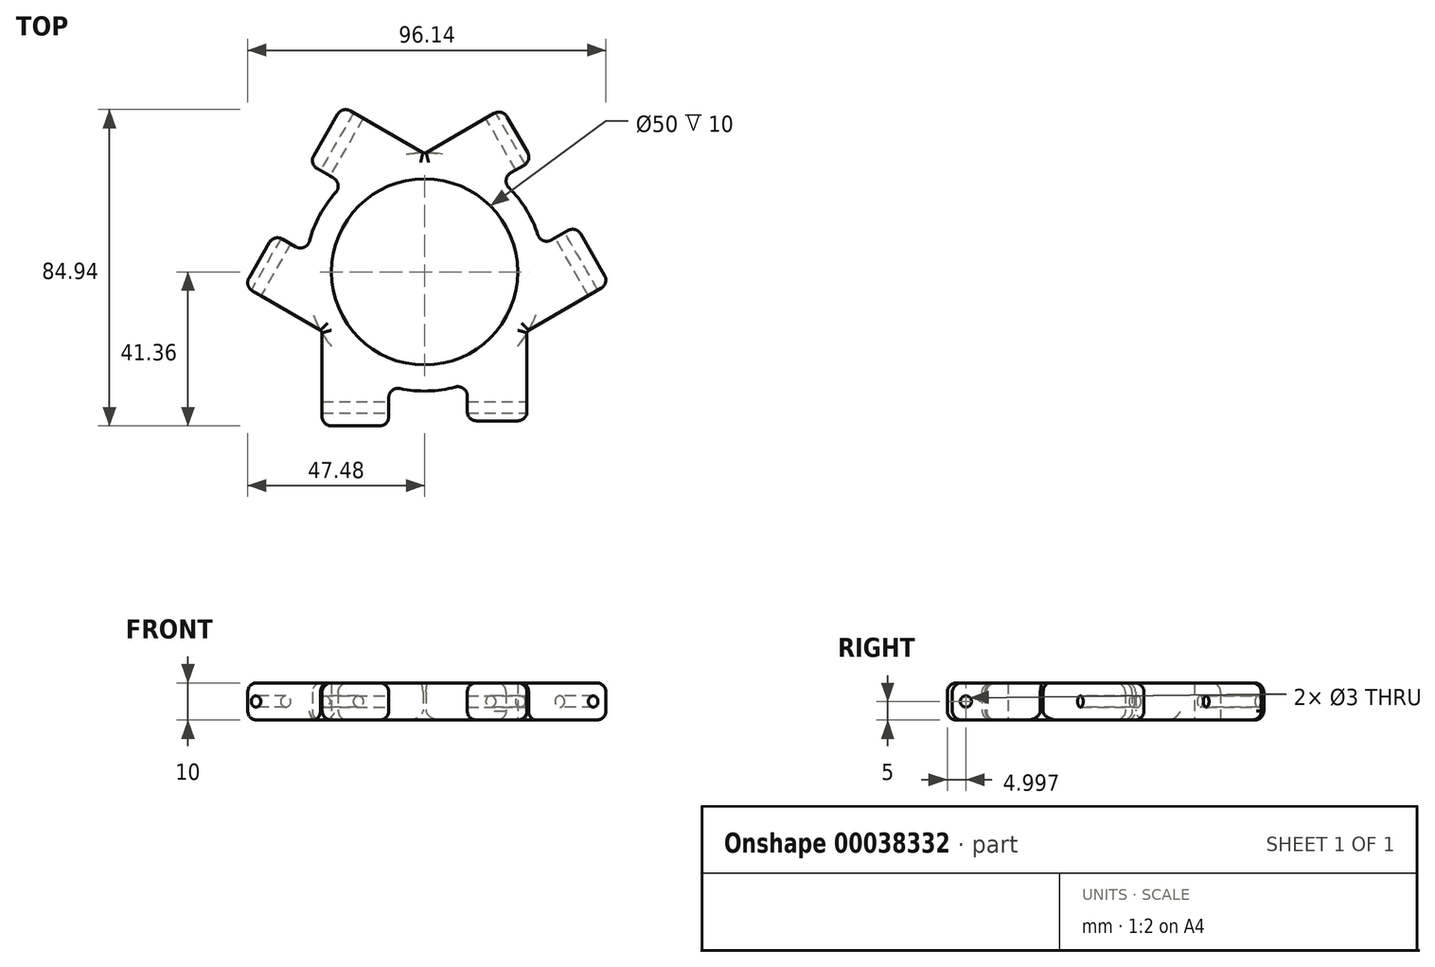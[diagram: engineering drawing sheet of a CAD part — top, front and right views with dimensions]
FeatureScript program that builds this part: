
annotation { "Feature Type Name" : "Feature", "Feature Type Description" : "" }
export const myFeature = defineFeature(function(context is Context, id is Id, definition is map)
    precondition{}
    {
        {
            var Q0;
            Q0=qCreatedBy(makeId("Top.planeOp"),FACE);
            var sketch = newSketch(context, id + "F0", { "sketchPlane" : qUnion([Q0])});
            skCircle(sketch, "E0", {"center": v(0, 0) * mm, "radius": 25 * mm});
            skCircle(sketch, "E1", {"center": v(0, 0) * mm, "radius": 32 * mm});
            skLineSegment(sketch, "E2", {"start": v(-9.6, -41.36) * mm, "end": v(-9.6, -30.53) * mm});
            skLineSegment(sketch, "E3", {"start": v(11.45, -29.88) * mm, "end": v(11.45, -40) * mm});
            skLineSegment(sketch, "E4", {"start": v(-27.5, -41.36) * mm, "end": v(-9.6, -41.36) * mm});
            skLineSegment(sketch, "E5", {"start": v(11.45, -40) * mm, "end": v(27.5, -40) * mm});
            skLineSegment(sketch, "E6", {"start": v(27.5, -40) * mm, "end": v(27.5, -16.36) * mm});
            skLineSegment(sketch, "E7", {"start": v(-27.5, -41.36) * mm, "end": v(-27.5, -16.36) * mm});
            skLineSegment(sketch, "E8.1.0", {"start": v(28.91, 29.92) * mm, "end": v(20.9, 43.82) * mm});
            skLineSegment(sketch, "E8.1.1", {"start": v(49.57, -3.13) * mm, "end": v(27.92, -15.63) * mm});
            skLineSegment(sketch, "E8.1.2", {"start": v(49.57, -3.13) * mm, "end": v(40.62, 12.37) * mm});
            skLineSegment(sketch, "E8.1.3", {"start": v(20.9, 43.82) * mm, "end": v(0.42, 32) * mm});
            skLineSegment(sketch, "E8.1.4", {"start": v(20.15, 24.86) * mm, "end": v(28.91, 29.92) * mm});
            skLineSegment(sketch, "E8.1.5", {"start": v(40.62, 12.37) * mm, "end": v(31.24, 6.95) * mm});
            skLineSegment(sketch, "E8.2.0", {"start": v(-40.37, 10.08) * mm, "end": v(-48.4, -3.82) * mm});
            skLineSegment(sketch, "E8.2.1", {"start": v(-22.07, 44.5) * mm, "end": v(-0.42, 32) * mm});
            skLineSegment(sketch, "E8.2.2", {"start": v(-22.07, 44.5) * mm, "end": v(-31.02, 29) * mm});
            skLineSegment(sketch, "E8.2.3", {"start": v(-48.4, -3.82) * mm, "end": v(-27.92, -15.63) * mm});
            skLineSegment(sketch, "E8.2.4", {"start": v(-31.6, 5.02) * mm, "end": v(-40.37, 10.08) * mm});
            skLineSegment(sketch, "E8.2.5", {"start": v(-31.02, 29) * mm, "end": v(-21.63, 23.58) * mm});
            skSolve(sketch);
        }
        {
            var Q0;
            Q0=makeQuery(id+"F0.imprint","IMPRINT",FACE,{"disambiguationData":[TD([[makeQuery(id+"F0.imprint","IMPRINT",EDGE,{"derivedFrom":sQuery(id+"F0.wireOp",EDGE,"E0")}),-1.0]])]});
            var Q1;
            Q1=makeQuery(id+"F0.imprint","IMPRINT",FACE,{"disambiguationData":[TD([[makeQuery(id+"F0.imprint","IMPRINT",EDGE,{"derivedFrom":sQuery(id+"F0.wireOp",EDGE,"E8.2.0")}),1.0]])]});
            var Q2;
            {var subQ1=sQuery(id+"F0.wireOp",EDGE,"E2");Q2=makeQuery(id+"F0.imprint","IMPRINT",FACE,{"disambiguationData":[TD([[makeQuery(id+"F0.imprint","IMPRINT",EDGE,{"derivedFrom":subQ1}),1.0]])]});}
            var Q3;
            {var subQ1=sQuery(id+"F0.wireOp",EDGE,"E8.2.1");Q3=makeQuery(id+"F0.imprint","IMPRINT",FACE,{"disambiguationData":[TD([[makeQuery(id+"F0.imprint","IMPRINT",EDGE,{"derivedFrom":subQ1}),-1.0]])]});}
            var Q4;
            Q4=makeQuery(id+"F0.imprint","IMPRINT",FACE,{"disambiguationData":[TD([[makeQuery(id+"F0.imprint","IMPRINT",EDGE,{"derivedFrom":sQuery(id+"F0.wireOp",EDGE,"E8.1.0")}),1.0]])]});
            var Q5;
            {var subQ1=sQuery(id+"F0.wireOp",EDGE,"E8.1.1");Q5=makeQuery(id+"F0.imprint","IMPRINT",FACE,{"disambiguationData":[TD([[makeQuery(id+"F0.imprint","IMPRINT",EDGE,{"derivedFrom":subQ1}),-1.0]])]});}
            var Q6;
            {var subQ0=sQuery(id+"F0.wireOp",EDGE,"E3");Q6=makeQuery(id+"F0.imprint","IMPRINT",FACE,{"disambiguationData":[TD([[makeQuery(id+"F0.imprint","IMPRINT",EDGE,{"derivedFrom":subQ0}),1.0]])]});}
            extrude(context, id + "F1", {"entities" : qUnion([Q0, Q1, Q2, Q3, Q4, Q5, Q6]), "depth" : 10 * mm});
        }
        {
            var Q0;
            Q0=makeQuery(id+"F1.opExtrude","SWEPT_FACE",FACE,{"disambiguationData":[OSD([sQuery(id+"F0.wireOp",EDGE,"E7")])]});
            var sketch = newSketch(context, id + "F2", { "sketchPlane" : qUnion([Q0])});
            skCircle(sketch, "E9", {"center": v(36.36, 5) * mm, "radius": 1.5 * mm});
            skSolve(sketch);
        }
        {
            var Q0;
            Q0=qSketchRegion(id+"F2",true);
            extrude(context, id + "F3", {"entities" : qUnion([Q0]), "depth" : 5 * mm, "hasSecondDirection" : true, "secondDirectionOppositeDirection" : true, "secondDirectionDepth" : 60 * mm});
        }
        {
            var Q0;
            Q0=makeQuery(id+"F3.opExtrude","SWEPT_BODY",BODY,{"disambiguationData":[OSD([sQuery(id+"F2.wireOp",EDGE,"E9")])]});
            var Q1;
            Q1=makeQuery(id+"F1.opExtrude","SWEPT_FACE",FACE,{"disambiguationData":[OSD([sQuery(id+"F0.wireOp",EDGE,"E0")])]});
            circularPattern(context, id + "F4", {"entities" : qUnion([Q0]), "axis" : qUnion([Q1]), "angle" : 120 * degree, "instanceCount" : round(3)});
        }
        {
            var Q0;
            Q0=makeQuery(id+"F3.opExtrude","SWEPT_BODY",BODY,{"disambiguationData":[OSD([sQuery(id+"F2.wireOp",EDGE,"E9")])]});
            var Q1;
            Q1=makeQuery(id+"F4.opPattern","COPY",BODY,{"derivedFrom":makeQuery(id+"F3.opExtrude","SWEPT_BODY",BODY,{"disambiguationData":[OSD([sQuery(id+"F2.wireOp",EDGE,"E9")])]}),"instanceName":"2"});
            var Q2;
            Q2=makeQuery(id+"F4.opPattern","COPY",BODY,{"derivedFrom":makeQuery(id+"F3.opExtrude","SWEPT_BODY",BODY,{"disambiguationData":[OSD([sQuery(id+"F2.wireOp",EDGE,"E9")])]}),"instanceName":"1"});
            var Q3;
            Q3=makeQuery(id+"F1.opExtrude","SWEPT_BODY",BODY,{"disambiguationData":[OSD([sQuery(id+"F0.wireOp",EDGE,"E0"),sQuery(id+"F0.wireOp",EDGE,"E1"),sQuery(id+"F0.wireOp",EDGE,"E2"),sQuery(id+"F0.wireOp",EDGE,"E3"),sQuery(id+"F0.wireOp",EDGE,"E4"),sQuery(id+"F0.wireOp",EDGE,"E5"),sQuery(id+"F0.wireOp",EDGE,"E6"),sQuery(id+"F0.wireOp",EDGE,"E7"),sQuery(id+"F0.wireOp",EDGE,"E8.1.0"),sQuery(id+"F0.wireOp",EDGE,"E8.1.1"),sQuery(id+"F0.wireOp",EDGE,"E8.1.2"),sQuery(id+"F0.wireOp",EDGE,"E8.1.3"),sQuery(id+"F0.wireOp",EDGE,"E8.1.4"),sQuery(id+"F0.wireOp",EDGE,"E8.1.5"),sQuery(id+"F0.wireOp",EDGE,"E8.2.0"),sQuery(id+"F0.wireOp",EDGE,"E8.2.1"),sQuery(id+"F0.wireOp",EDGE,"E8.2.2"),sQuery(id+"F0.wireOp",EDGE,"E8.2.3"),sQuery(id+"F0.wireOp",EDGE,"E8.2.4"),sQuery(id+"F0.wireOp",EDGE,"E8.2.5")])]});
            booleanBodies(context, id + "F5", {"operationType" : BooleanOperationType.SUBTRACTION, "tools" : qUnion([Q0, Q1, Q2]), "targets" : qUnion([Q3])});
        }
        {
            var Q0;
            Q0=makeQuery(id+"F1.opExtrude","CAP_EDGE",EDGE,{"disambiguationData":[OSD([sQuery(id+"F0.wireOp",EDGE,"E8.2.3")])],"isStart":false});
            var Q1;
            Q1=makeQuery(id+"F1.opExtrude","CAP_EDGE",EDGE,{"disambiguationData":[OSD([sQuery(id+"F0.wireOp",EDGE,"E8.2.0")])],"isStart":false});
            var Q2;
            Q2=makeQuery(id+"F1.opExtrude","SWEPT_EDGE",EDGE,{"disambiguationData":[OSD([sQuery(id+"F0.wireOp",EDGE,"E8.2.0"),sQuery(id+"F0.wireOp",EDGE,"E8.2.3")])]});
            var Q3;
            Q3=makeQuery(id+"F1.opExtrude","CAP_EDGE",EDGE,{"disambiguationData":[OSD([sQuery(id+"F0.wireOp",EDGE,"E8.2.4")])],"isStart":false});
            var Q4;
            Q4=makeQuery(id+"F1.opExtrude","SWEPT_EDGE",EDGE,{"disambiguationData":[OSD([sQuery(id+"F0.wireOp",EDGE,"E8.2.0"),sQuery(id+"F0.wireOp",EDGE,"E8.2.4")])]});
            var Q5;
            Q5=makeQuery(id+"F1.opExtrude","CAP_EDGE",EDGE,{"disambiguationData":[OSD([sQuery(id+"F0.wireOp",EDGE,"E8.2.4")])],"isStart":true});
            var Q6;
            {var subQ0=sQuery(id+"F0.wireOp",EDGE,"E1");Q6=makeQuery(id+"F1.opExtrude","CAP_EDGE",EDGE,{"disambiguationData":[OSD([subQ0]),TDD([makeQuery(id+"F0.imprint","IMPRINT",EDGE,{"disambiguationData":[TD([[makeQuery(id+"F0.imprint","INTERSECT",VERTEX,{"derivedFrom":[subQ0,sQuery(id+"F0.wireOp",EDGE,"E8.2.4")]}),1.0]])],"derivedFrom":subQ0})])],"isStart":false});}
            var Q7;
            Q7=makeQuery(id+"F1.opExtrude","CAP_EDGE",EDGE,{"disambiguationData":[OSD([sQuery(id+"F0.wireOp",EDGE,"E8.2.5")])],"isStart":false});
            var Q8;
            Q8=makeQuery(id+"F1.opExtrude","CAP_EDGE",EDGE,{"disambiguationData":[OSD([sQuery(id+"F0.wireOp",EDGE,"E8.2.2")])],"isStart":false});
            var Q9;
            Q9=makeQuery(id+"F1.opExtrude","SWEPT_EDGE",EDGE,{"disambiguationData":[OSD([sQuery(id+"F0.wireOp",EDGE,"E8.2.2"),sQuery(id+"F0.wireOp",EDGE,"E8.2.5")])]});
            var Q10;
            Q10=makeQuery(id+"F1.opExtrude","SWEPT_EDGE",EDGE,{"disambiguationData":[OSD([sQuery(id+"F0.wireOp",EDGE,"E8.2.1"),sQuery(id+"F0.wireOp",EDGE,"E8.2.2")])]});
            var Q11;
            Q11=makeQuery(id+"F1.opExtrude","CAP_EDGE",EDGE,{"disambiguationData":[OSD([sQuery(id+"F0.wireOp",EDGE,"E8.2.1")])],"isStart":false});
            var Q12;
            Q12=makeQuery(id+"F1.opExtrude","CAP_EDGE",EDGE,{"disambiguationData":[OSD([sQuery(id+"F0.wireOp",EDGE,"E8.1.3")])],"isStart":false});
            var Q13;
            {var subQ0=sQuery(id+"F0.wireOp",EDGE,"E1");Q13=makeQuery(id+"F1.opExtrude","CAP_EDGE",EDGE,{"disambiguationData":[OSD([subQ0]),TDD([makeQuery(id+"F0.imprint","IMPRINT",EDGE,{"disambiguationData":[TD([[makeQuery(id+"F0.imprint","INTERSECT",VERTEX,{"derivedFrom":[subQ0,sQuery(id+"F0.wireOp",EDGE,"E8.1.4")]}),1.0]])],"derivedFrom":subQ0})])],"isStart":false});}
            var Q14;
            Q14=makeQuery(id+"F1.opExtrude","CAP_EDGE",EDGE,{"disambiguationData":[OSD([sQuery(id+"F0.wireOp",EDGE,"E8.1.0")])],"isStart":false});
            var Q15;
            Q15=makeQuery(id+"F1.opExtrude","CAP_EDGE",EDGE,{"disambiguationData":[OSD([sQuery(id+"F0.wireOp",EDGE,"E8.1.0")])],"isStart":true});
            var Q16;
            Q16=makeQuery(id+"F1.opExtrude","SWEPT_EDGE",EDGE,{"disambiguationData":[OSD([sQuery(id+"F0.wireOp",EDGE,"E8.1.0"),sQuery(id+"F0.wireOp",EDGE,"E8.1.3")])]});
            var Q17;
            Q17=makeQuery(id+"F1.opExtrude","CAP_EDGE",EDGE,{"disambiguationData":[OSD([sQuery(id+"F0.wireOp",EDGE,"E8.2.1")])],"isStart":true});
            var Q18;
            {var subQ0=sQuery(id+"F0.wireOp",EDGE,"E1");Q18=makeQuery(id+"F1.opExtrude","CAP_EDGE",EDGE,{"disambiguationData":[OSD([subQ0]),TDD([makeQuery(id+"F0.imprint","IMPRINT",EDGE,{"disambiguationData":[TD([[makeQuery(id+"F0.imprint","INTERSECT",VERTEX,{"derivedFrom":[subQ0,sQuery(id+"F0.wireOp",EDGE,"E8.1.4")]}),1.0]])],"derivedFrom":subQ0})])],"isStart":true});}
            var Q19;
            Q19=makeQuery(id+"F1.opExtrude","SWEPT_EDGE",EDGE,{"disambiguationData":[OSD([sQuery(id+"F0.wireOp",EDGE,"E8.1.0"),sQuery(id+"F0.wireOp",EDGE,"E8.1.4")])]});
            var Q20;
            Q20=makeQuery(id+"F1.opExtrude","CAP_EDGE",EDGE,{"disambiguationData":[OSD([sQuery(id+"F0.wireOp",EDGE,"E8.1.4")])],"isStart":false});
            var Q21;
            Q21=makeQuery(id+"F1.opExtrude","CAP_EDGE",EDGE,{"disambiguationData":[OSD([sQuery(id+"F0.wireOp",EDGE,"E8.1.5")])],"isStart":false});
            var Q22;
            Q22=makeQuery(id+"F1.opExtrude","CAP_EDGE",EDGE,{"disambiguationData":[OSD([sQuery(id+"F0.wireOp",EDGE,"E8.1.2")])],"isStart":false});
            var Q23;
            Q23=makeQuery(id+"F1.opExtrude","CAP_EDGE",EDGE,{"disambiguationData":[OSD([sQuery(id+"F0.wireOp",EDGE,"E8.1.2")])],"isStart":true});
            var Q24;
            Q24=makeQuery(id+"F1.opExtrude","SWEPT_EDGE",EDGE,{"disambiguationData":[OSD([sQuery(id+"F0.wireOp",EDGE,"E8.1.1"),sQuery(id+"F0.wireOp",EDGE,"E8.1.2")])]});
            var Q25;
            Q25=makeQuery(id+"F1.opExtrude","SWEPT_EDGE",EDGE,{"disambiguationData":[OSD([sQuery(id+"F0.wireOp",EDGE,"E8.1.2"),sQuery(id+"F0.wireOp",EDGE,"E8.1.5")])]});
            var Q26;
            Q26=makeQuery(id+"F1.opExtrude","CAP_EDGE",EDGE,{"disambiguationData":[OSD([sQuery(id+"F0.wireOp",EDGE,"E8.1.1")])],"isStart":false});
            var Q27;
            Q27=makeQuery(id+"F1.opExtrude","CAP_EDGE",EDGE,{"disambiguationData":[OSD([sQuery(id+"F0.wireOp",EDGE,"E8.1.1")])],"isStart":true});
            var Q28;
            Q28=makeQuery(id+"F1.opExtrude","CAP_EDGE",EDGE,{"disambiguationData":[OSD([sQuery(id+"F0.wireOp",EDGE,"E6")])],"isStart":false});
            var Q29;
            Q29=makeQuery(id+"F1.opExtrude","CAP_EDGE",EDGE,{"disambiguationData":[OSD([sQuery(id+"F0.wireOp",EDGE,"E6")])],"isStart":true});
            var Q30;
            Q30=makeQuery(id+"F1.opExtrude","SWEPT_EDGE",EDGE,{"disambiguationData":[OSD([sQuery(id+"F0.wireOp",EDGE,"E5"),sQuery(id+"F0.wireOp",EDGE,"E6")])]});
            var Q31;
            Q31=makeQuery(id+"F1.opExtrude","CAP_EDGE",EDGE,{"disambiguationData":[OSD([sQuery(id+"F0.wireOp",EDGE,"E5")])],"isStart":false});
            var Q32;
            Q32=makeQuery(id+"F1.opExtrude","CAP_EDGE",EDGE,{"disambiguationData":[OSD([sQuery(id+"F0.wireOp",EDGE,"E3")])],"isStart":false});
            var Q33;
            Q33=makeQuery(id+"F1.opExtrude","CAP_EDGE",EDGE,{"disambiguationData":[OSD([sQuery(id+"F0.wireOp",EDGE,"E5")])],"isStart":true});
            var Q34;
            Q34=makeQuery(id+"F1.opExtrude","SWEPT_EDGE",EDGE,{"disambiguationData":[OSD([sQuery(id+"F0.wireOp",EDGE,"E3"),sQuery(id+"F0.wireOp",EDGE,"E5")])]});
            var Q35;
            {var subQ0=sQuery(id+"F0.wireOp",EDGE,"E1");Q35=makeQuery(id+"F1.opExtrude","CAP_EDGE",EDGE,{"disambiguationData":[OSD([subQ0]),TDD([makeQuery(id+"F0.imprint","IMPRINT",EDGE,{"disambiguationData":[TD([[makeQuery(id+"F0.imprint","INTERSECT",VERTEX,{"derivedFrom":[subQ0,sQuery(id+"F0.wireOp",EDGE,"E2")]}),-1.0]])],"derivedFrom":subQ0})])],"isStart":false});}
            var Q36;
            {var subQ0=sQuery(id+"F0.wireOp",EDGE,"E1");Q36=makeQuery(id+"F1.opExtrude","CAP_EDGE",EDGE,{"disambiguationData":[OSD([subQ0]),TDD([makeQuery(id+"F0.imprint","IMPRINT",EDGE,{"disambiguationData":[TD([[makeQuery(id+"F0.imprint","INTERSECT",VERTEX,{"derivedFrom":[subQ0,sQuery(id+"F0.wireOp",EDGE,"E2")]}),-1.0]])],"derivedFrom":subQ0})])],"isStart":true});}
            var Q37;
            Q37=makeQuery(id+"F1.opExtrude","CAP_EDGE",EDGE,{"disambiguationData":[OSD([sQuery(id+"F0.wireOp",EDGE,"E2")])],"isStart":false});
            var Q38;
            Q38=makeQuery(id+"F1.opExtrude","CAP_EDGE",EDGE,{"disambiguationData":[OSD([sQuery(id+"F0.wireOp",EDGE,"E2")])],"isStart":true});
            var Q39;
            Q39=makeQuery(id+"F1.opExtrude","CAP_EDGE",EDGE,{"disambiguationData":[OSD([sQuery(id+"F0.wireOp",EDGE,"E4")])],"isStart":true});
            var Q40;
            Q40=makeQuery(id+"F1.opExtrude","CAP_EDGE",EDGE,{"disambiguationData":[OSD([sQuery(id+"F0.wireOp",EDGE,"E4")])],"isStart":false});
            var Q41;
            Q41=makeQuery(id+"F1.opExtrude","CAP_EDGE",EDGE,{"disambiguationData":[OSD([sQuery(id+"F0.wireOp",EDGE,"E7")])],"isStart":false});
            var Q42;
            Q42=makeQuery(id+"F1.opExtrude","CAP_EDGE",EDGE,{"disambiguationData":[OSD([sQuery(id+"F0.wireOp",EDGE,"E7")])],"isStart":true});
            var Q43;
            Q43=makeQuery(id+"F1.opExtrude","CAP_EDGE",EDGE,{"disambiguationData":[OSD([sQuery(id+"F0.wireOp",EDGE,"E8.2.3")])],"isStart":true});
            var Q44;
            Q44=makeQuery(id+"F1.opExtrude","CAP_EDGE",EDGE,{"disambiguationData":[OSD([sQuery(id+"F0.wireOp",EDGE,"E8.2.2")])],"isStart":true});
            var Q45;
            Q45=makeQuery(id+"F1.opExtrude","CAP_EDGE",EDGE,{"disambiguationData":[OSD([sQuery(id+"F0.wireOp",EDGE,"E8.2.5")])],"isStart":true});
            var Q46;
            Q46=makeQuery(id+"F1.opExtrude","CAP_EDGE",EDGE,{"disambiguationData":[OSD([sQuery(id+"F0.wireOp",EDGE,"E8.1.3")])],"isStart":true});
            var Q47;
            Q47=makeQuery(id+"F1.opExtrude","CAP_EDGE",EDGE,{"disambiguationData":[OSD([sQuery(id+"F0.wireOp",EDGE,"E3")])],"isStart":true});
            var Q48;
            Q48=makeQuery(id+"F1.opExtrude","CAP_EDGE",EDGE,{"disambiguationData":[OSD([sQuery(id+"F0.wireOp",EDGE,"E8.1.5")])],"isStart":true});
            var Q49;
            Q49=makeQuery(id+"F1.opExtrude","CAP_EDGE",EDGE,{"disambiguationData":[OSD([sQuery(id+"F0.wireOp",EDGE,"E8.1.4")])],"isStart":true});
            var Q50;
            {var subQ0=sQuery(id+"F0.wireOp",EDGE,"E1");Q50=makeQuery(id+"F1.opExtrude","CAP_EDGE",EDGE,{"disambiguationData":[OSD([subQ0]),TDD([makeQuery(id+"F0.imprint","IMPRINT",EDGE,{"disambiguationData":[TD([[makeQuery(id+"F0.imprint","INTERSECT",VERTEX,{"derivedFrom":[subQ0,sQuery(id+"F0.wireOp",EDGE,"E8.1.3")]}),-1.0]])],"derivedFrom":subQ0})])],"isStart":false});}
            var Q51;
            {var subQ0=sQuery(id+"F0.wireOp",EDGE,"E1");Q51=makeQuery(id+"F1.opExtrude","CAP_EDGE",EDGE,{"disambiguationData":[OSD([subQ0]),TDD([makeQuery(id+"F0.imprint","IMPRINT",EDGE,{"disambiguationData":[TD([[makeQuery(id+"F0.imprint","INTERSECT",VERTEX,{"derivedFrom":[subQ0,sQuery(id+"F0.wireOp",EDGE,"E7")]}),1.0]])],"derivedFrom":subQ0})])],"isStart":false});}
            var Q52;
            {var subQ0=sQuery(id+"F0.wireOp",EDGE,"E1");Q52=makeQuery(id+"F1.opExtrude","CAP_EDGE",EDGE,{"disambiguationData":[OSD([subQ0]),TDD([makeQuery(id+"F0.imprint","IMPRINT",EDGE,{"disambiguationData":[TD([[makeQuery(id+"F0.imprint","INTERSECT",VERTEX,{"derivedFrom":[subQ0,sQuery(id+"F0.wireOp",EDGE,"E6")]}),-1.0]])],"derivedFrom":subQ0})])],"isStart":false});}
            var Q53;
            Q53=makeQuery(id+"F1.opExtrude","CAP_EDGE",EDGE,{"disambiguationData":[OSD([sQuery(id+"F0.wireOp",EDGE,"E8.2.0")])],"isStart":true});
            var Q54;
            Q54=makeQuery(id+"F1.opExtrude","SWEPT_EDGE",EDGE,{"disambiguationData":[OSD([sQuery(id+"F0.wireOp",EDGE,"E4"),sQuery(id+"F0.wireOp",EDGE,"E7")])]});
            var Q55;
            Q55=makeQuery(id+"F1.opExtrude","SWEPT_EDGE",EDGE,{"disambiguationData":[OSD([sQuery(id+"F0.wireOp",EDGE,"E2"),sQuery(id+"F0.wireOp",EDGE,"E4")])]});
            var Q56;
            Q56=makeQuery(id+"F1.opExtrude","SWEPT_EDGE",EDGE,{"disambiguationData":[OSD([sQuery(id+"F0.wireOp",EDGE,"E1"),sQuery(id+"F0.wireOp",EDGE,"E8.1.5")])]});
            var Q57;
            Q57=makeQuery(id+"F1.opExtrude","SWEPT_EDGE",EDGE,{"disambiguationData":[OSD([sQuery(id+"F0.wireOp",EDGE,"E1"),sQuery(id+"F0.wireOp",EDGE,"E8.1.4")])]});
            var Q58;
            Q58=makeQuery(id+"F1.opExtrude","SWEPT_EDGE",EDGE,{"disambiguationData":[OSD([sQuery(id+"F0.wireOp",EDGE,"E1"),sQuery(id+"F0.wireOp",EDGE,"E8.2.5")])]});
            var Q59;
            Q59=makeQuery(id+"F1.opExtrude","SWEPT_EDGE",EDGE,{"disambiguationData":[OSD([sQuery(id+"F0.wireOp",EDGE,"E1"),sQuery(id+"F0.wireOp",EDGE,"E8.2.4")])]});
            var Q60;
            Q60=makeQuery(id+"F1.opExtrude","SWEPT_EDGE",EDGE,{"disambiguationData":[OSD([sQuery(id+"F0.wireOp",EDGE,"E1"),sQuery(id+"F0.wireOp",EDGE,"E2")])]});
            var Q61;
            Q61=makeQuery(id+"F1.opExtrude","SWEPT_EDGE",EDGE,{"disambiguationData":[OSD([sQuery(id+"F0.wireOp",EDGE,"E1"),sQuery(id+"F0.wireOp",EDGE,"E3")])]});
            fillet(context, id + "F6", {"entities" : qUnion([Q0, Q1, Q2, Q3, Q4, Q5, Q6, Q7, Q8, Q9, Q10, Q11, Q12, Q13, Q14, Q15, Q16, Q17, Q18, Q19, Q20, Q21, Q22, Q23, Q24, Q25, Q26, Q27, Q28, Q29, Q30, Q31, Q32, Q33, Q34, Q35, Q36, Q37, Q38, Q39, Q40, Q41, Q42, Q43, Q44, Q45, Q46, Q47, Q48, Q49, Q50, Q51, Q52, Q53, Q54, Q55, Q56, Q57, Q58, Q59, Q60, Q61]), "radius" : 2.5 * mm, "tangentPropagation" : true, "allowEdgeOverflow" : false});
        }
    });
